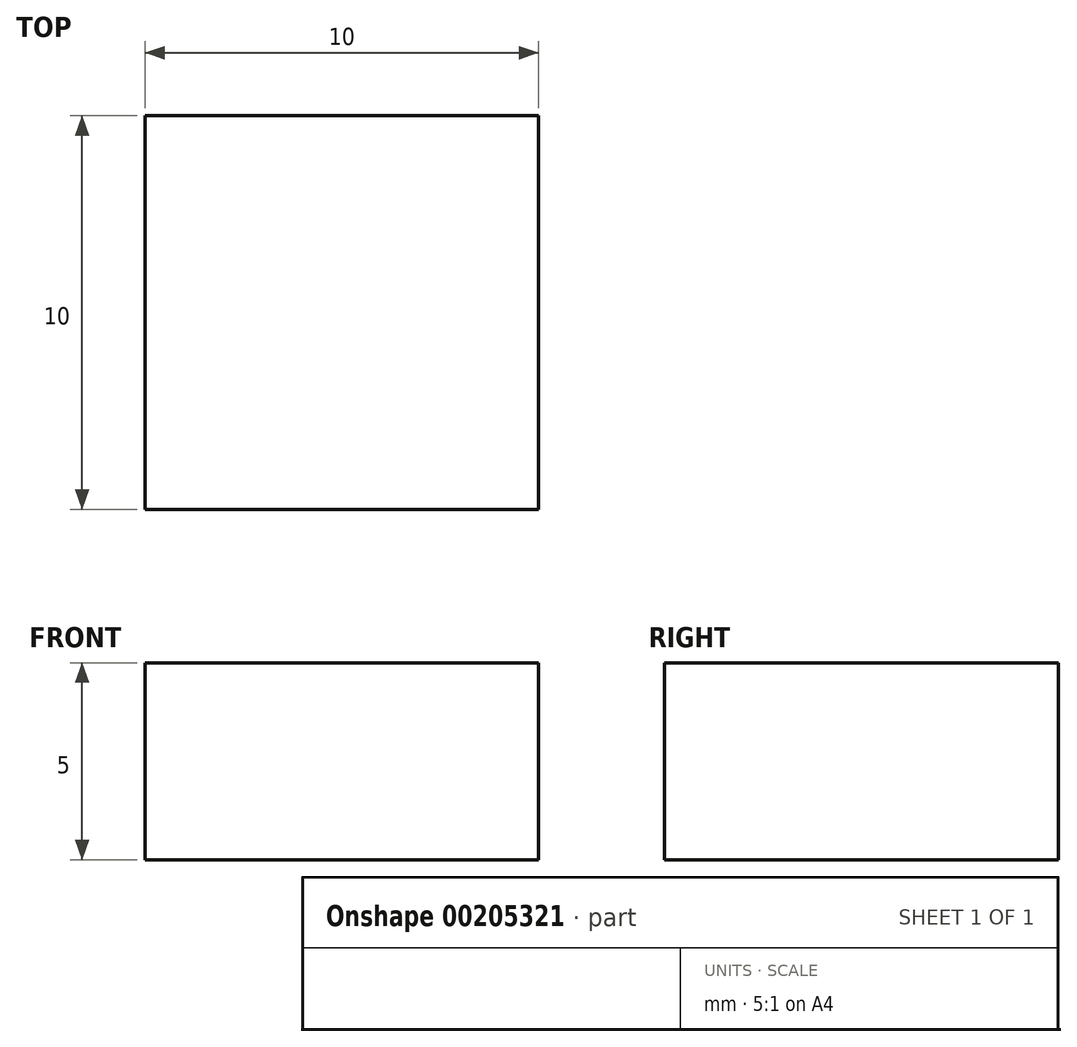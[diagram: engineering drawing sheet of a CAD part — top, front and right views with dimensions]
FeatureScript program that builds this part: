
annotation { "Feature Type Name" : "Feature", "Feature Type Description" : "" }
export const myFeature = defineFeature(function(context is Context, id is Id, definition is map)
    precondition{}
    {
        {
            var Q0;
            Q0=qCreatedBy(makeId("Top.planeOp"),FACE);
            var sketch = newSketch(context, id + "F0", { "sketchPlane" : qUnion([Q0])});
            skLineSegment(sketch, "E0.bottom", {"start": v(0, 0) * mm, "end": v(10, 0) * mm});
            skLineSegment(sketch, "E0.top", {"start": v(0, 10) * mm, "end": v(10, 10) * mm});
            skLineSegment(sketch, "E0.left", {"start": v(0, 0) * mm, "end": v(0, 10) * mm});
            skLineSegment(sketch, "E0.right", {"start": v(10, 0) * mm, "end": v(10, 10) * mm});
            skSolve(sketch);
        }
        {
            var Q0;
            Q0=qSketchRegion(id+"F0",true);
            extrude(context, id + "F1", {"entities" : qUnion([Q0]), "depth" : 5 * mm});
        }
    });
